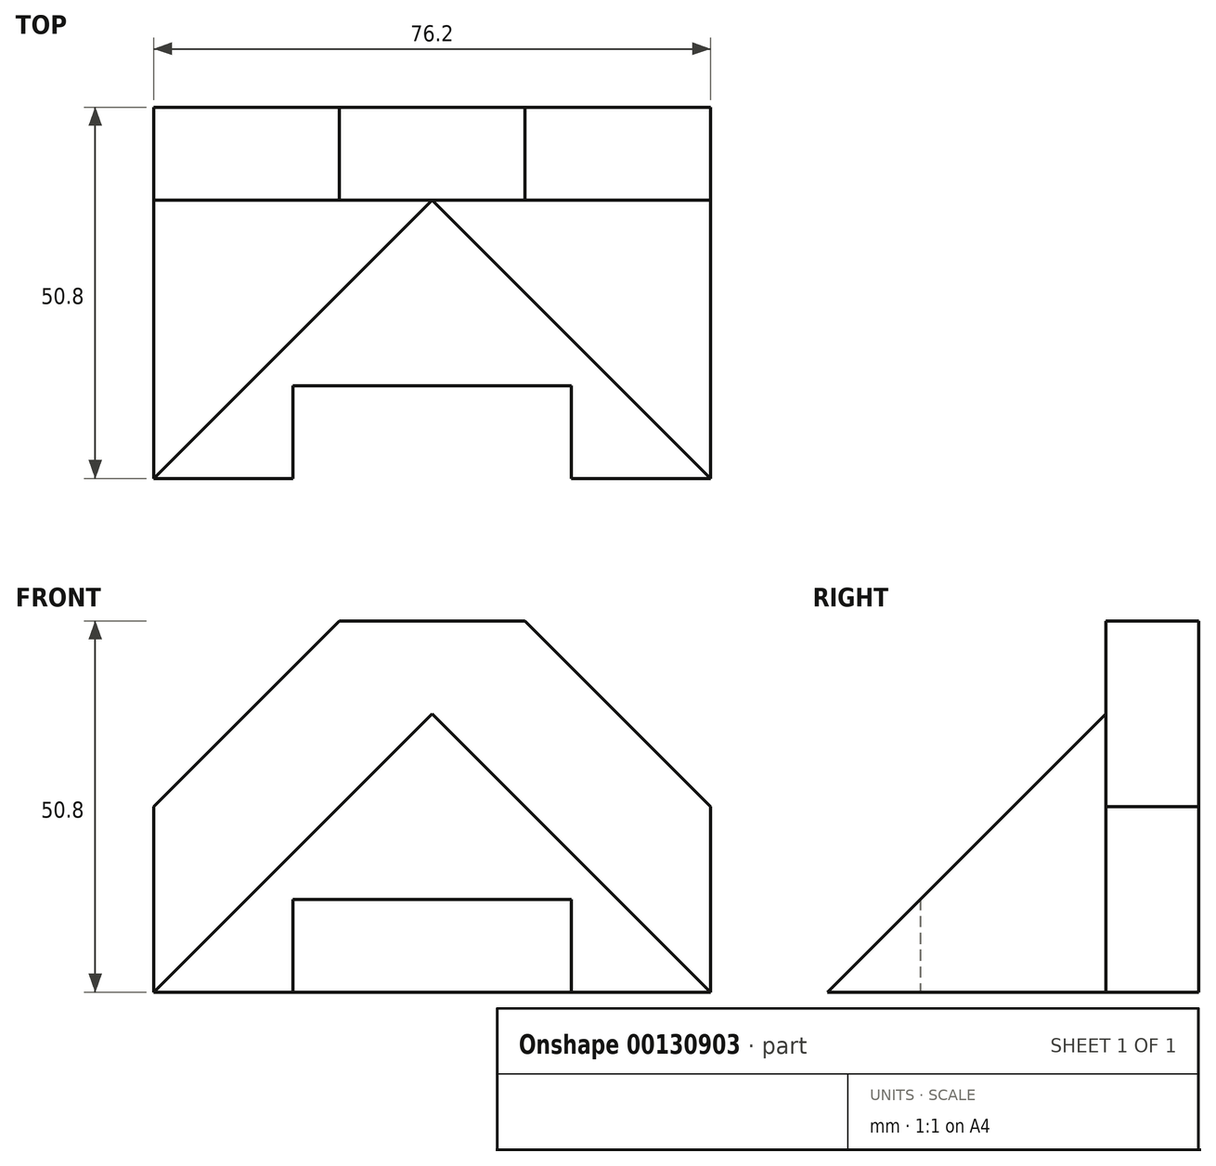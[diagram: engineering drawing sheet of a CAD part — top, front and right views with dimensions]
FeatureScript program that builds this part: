
annotation { "Feature Type Name" : "Feature", "Feature Type Description" : "" }
export const myFeature = defineFeature(function(context is Context, id is Id, definition is map)
    precondition{}
    {
        {
            var Q0;
            Q0=qCreatedBy(makeId("Front.planeOp"),FACE);
            var sketch = newSketch(context, id + "F0", { "sketchPlane" : qUnion([Q0])});
            skLineSegment(sketch, "E0", {"start": v(-38.1, 0) * mm, "end": v(0, 0) * mm});
            skLineSegment(sketch, "E1", {"start": v(0, 0) * mm, "end": v(38.1, 0) * mm});
            skLineSegment(sketch, "E2", {"start": v(38.1, 0) * mm, "end": v(0, 38.1) * mm});
            skLineSegment(sketch, "E3", {"start": v(0, 38.1) * mm, "end": v(-38.1, 0) * mm});
            skSolve(sketch);
        }
        {
            var Q0;
            Q0=qSketchRegion(id+"F0",true);
            extrude(context, id + "F1", {"entities" : qUnion([Q0]), "depth" : 38.1 * mm});
        }
        {
            var Q0;
            Q0=qCreatedBy(makeId("Right.planeOp"),FACE);
            var sketch = newSketch(context, id + "F2", { "sketchPlane" : qUnion([Q0])});
            skLineSegment(sketch, "E4", {"start": v(0, 38.1) * mm, "end": v(-38.1, 0) * mm});
            skLineSegment(sketch, "E5", {"start": v(-38.1, 0) * mm, "end": v(-38.1, 38.1) * mm});
            skLineSegment(sketch, "E6", {"start": v(-38.1, 38.1) * mm, "end": v(0, 38.1) * mm});
            skSolve(sketch);
        }
        {
            var Q0;
            Q0=qSketchRegion(id+"F2",true);
            extrude(context, id + "F3", {"entities" : qUnion([Q0]), "operationType" : NewBodyOperationType.REMOVE, "endBound" : BoundingType.SYMMETRIC, "depth" : 6 * 12.95 * mm});
        }
        {
            var Q0;
            Q0=qCreatedBy(makeId("Top.planeOp"),FACE);
            var sketch = newSketch(context, id + "F4", { "sketchPlane" : qUnion([Q0])});
            skLineSegment(sketch, "E7", {"start": v(0, -38.1) * mm, "end": v(19.05, -38.1) * mm});
            skLineSegment(sketch, "E8", {"start": v(19.05, -38.1) * mm, "end": v(19.05, -25.4) * mm});
            skLineSegment(sketch, "E9", {"start": v(19.05, -25.4) * mm, "end": v(-19.05, -25.4) * mm});
            skLineSegment(sketch, "E10", {"start": v(-19.05, -25.4) * mm, "end": v(-19.05, -38.1) * mm});
            skLineSegment(sketch, "E11", {"start": v(-19.05, -38.1) * mm, "end": v(0, -38.1) * mm});
            skSolve(sketch);
        }
        {
            var Q0;
            Q0=qSketchRegion(id+"F4",true);
            extrude(context, id + "F5", {"entities" : qUnion([Q0]), "operationType" : NewBodyOperationType.REMOVE, "endBound" : BoundingType.THROUGH_ALL, "depth" : 25.4 * mm});
        }
        {
            var Q0;
            Q0=makeQuery(id+"F1.opExtrude","CAP_FACE",FACE,{"disambiguationData":[OSD([sQuery(id+"F0.wireOp",EDGE,"E0"),sQuery(id+"F0.wireOp",EDGE,"E1"),sQuery(id+"F0.wireOp",EDGE,"E2"),sQuery(id+"F0.wireOp",EDGE,"E3")])],"isStart":true});
            var sketch = newSketch(context, id + "F6", { "sketchPlane" : qUnion([Q0])});
            skLineSegment(sketch, "E12", {"start": v(0, 0) * mm, "end": v(38.1, 0) * mm});
            skLineSegment(sketch, "E13", {"start": v(38.1, 0) * mm, "end": v(38.1, 25.4) * mm});
            skLineSegment(sketch, "E14", {"start": v(38.1, 25.4) * mm, "end": v(12.7, 50.8) * mm});
            skLineSegment(sketch, "E15", {"start": v(12.7, 50.8) * mm, "end": v(-12.7, 50.8) * mm});
            skLineSegment(sketch, "E16", {"start": v(-12.7, 50.8) * mm, "end": v(-38.1, 25.4) * mm});
            skLineSegment(sketch, "E17", {"start": v(-38.1, 25.4) * mm, "end": v(-38.1, 0) * mm});
            skLineSegment(sketch, "E18", {"start": v(-38.1, 0) * mm, "end": v(0, 0) * mm});
            skSolve(sketch);
        }
        {
            var Q0;
            Q0=qSketchRegion(id+"F6",true);
            extrude(context, id + "F7", {"entities" : qUnion([Q0]), "operationType" : NewBodyOperationType.ADD, "depth" : 12.7 * mm});
        }
    });
